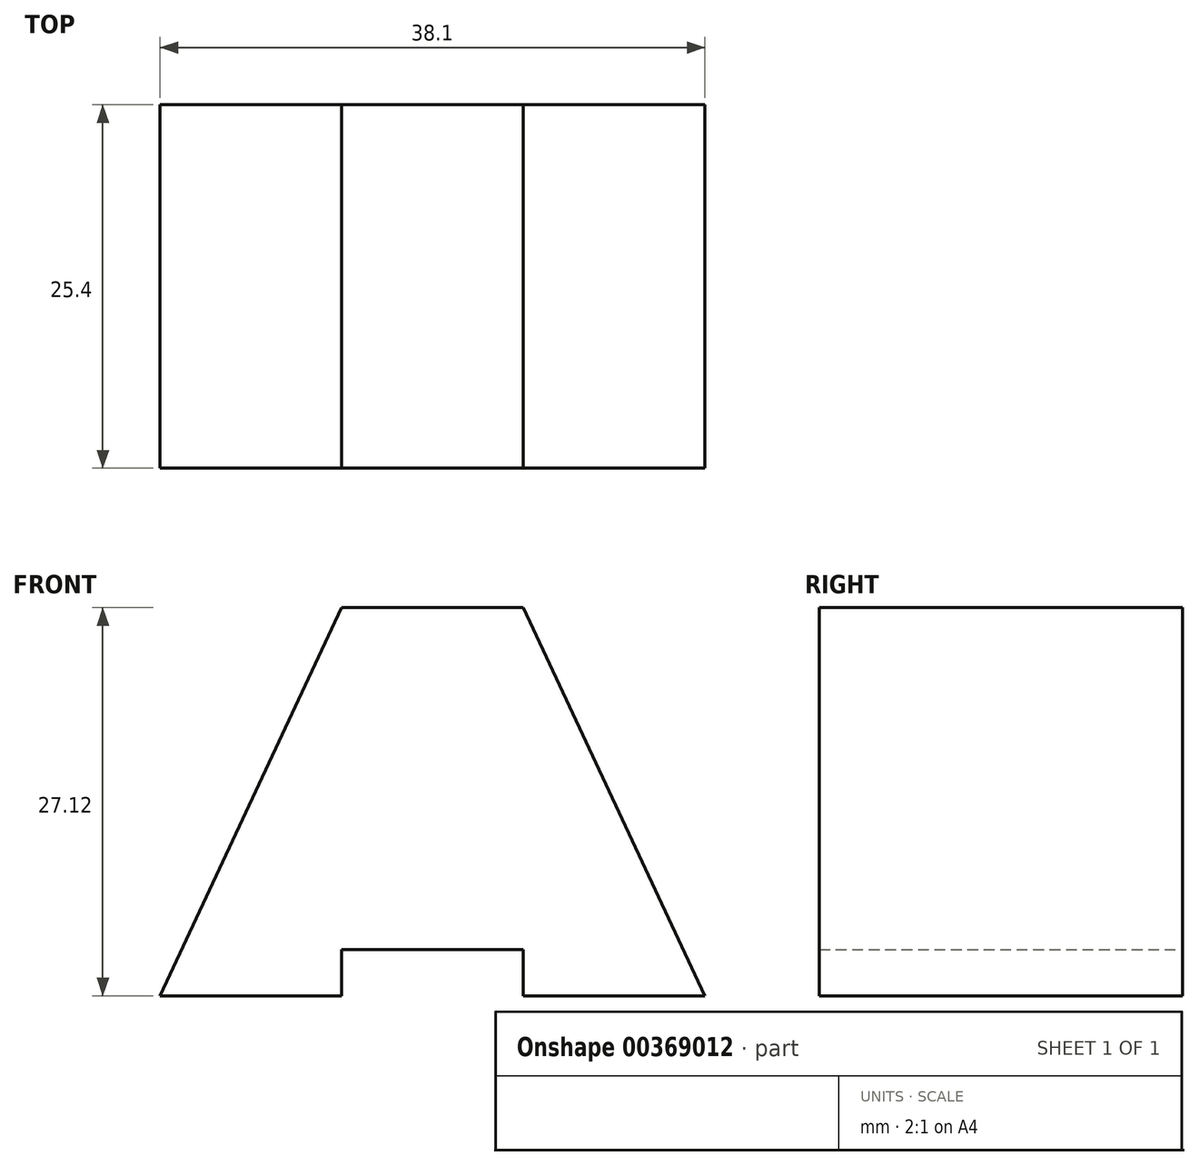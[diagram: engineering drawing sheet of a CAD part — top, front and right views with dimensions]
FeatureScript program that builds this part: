
annotation { "Feature Type Name" : "Feature", "Feature Type Description" : "" }
export const myFeature = defineFeature(function(context is Context, id is Id, definition is map)
    precondition{}
    {
        {
            var Q0;
            Q0=qCreatedBy(makeId("Front.planeOp"),FACE);
            var sketch = newSketch(context, id + "F0", { "sketchPlane" : qUnion([Q0])});
            skLineSegment(sketch, "E0", {"start": v(-25.4, 0) * mm, "end": v(-12.7, 27.12) * mm});
            skLineSegment(sketch, "E1", {"start": v(-12.7, 27.12) * mm, "end": v(0, 27.12) * mm});
            skLineSegment(sketch, "E2", {"start": v(0, 27.12) * mm, "end": v(12.7, 0) * mm});
            skLineSegment(sketch, "E3", {"start": v(12.7, 0) * mm, "end": v(0, 0) * mm});
            skLineSegment(sketch, "E4", {"start": v(0, 0) * mm, "end": v(0, 3.21) * mm});
            skLineSegment(sketch, "E5", {"start": v(0, 3.21) * mm, "end": v(-12.7, 3.21) * mm});
            skLineSegment(sketch, "E6", {"start": v(-12.7, 3.21) * mm, "end": v(-12.7, 0) * mm});
            skLineSegment(sketch, "E7", {"start": v(-12.7, 0) * mm, "end": v(-25.4, 0) * mm});
            skSolve(sketch);
        }
        {
            var Q0;
            Q0=makeQuery(id+"F0.imprint","IMPRINT",FACE,{"disambiguationData":[TD([[makeQuery(id+"F0.imprint","IMPRINT",EDGE,{"derivedFrom":sQuery(id+"F0.wireOp",EDGE,"E0")}),-1.0]])]});
            extrude(context, id + "F1", {"entities" : qUnion([Q0]), "depth" : 25.4 * mm});
        }
    });
